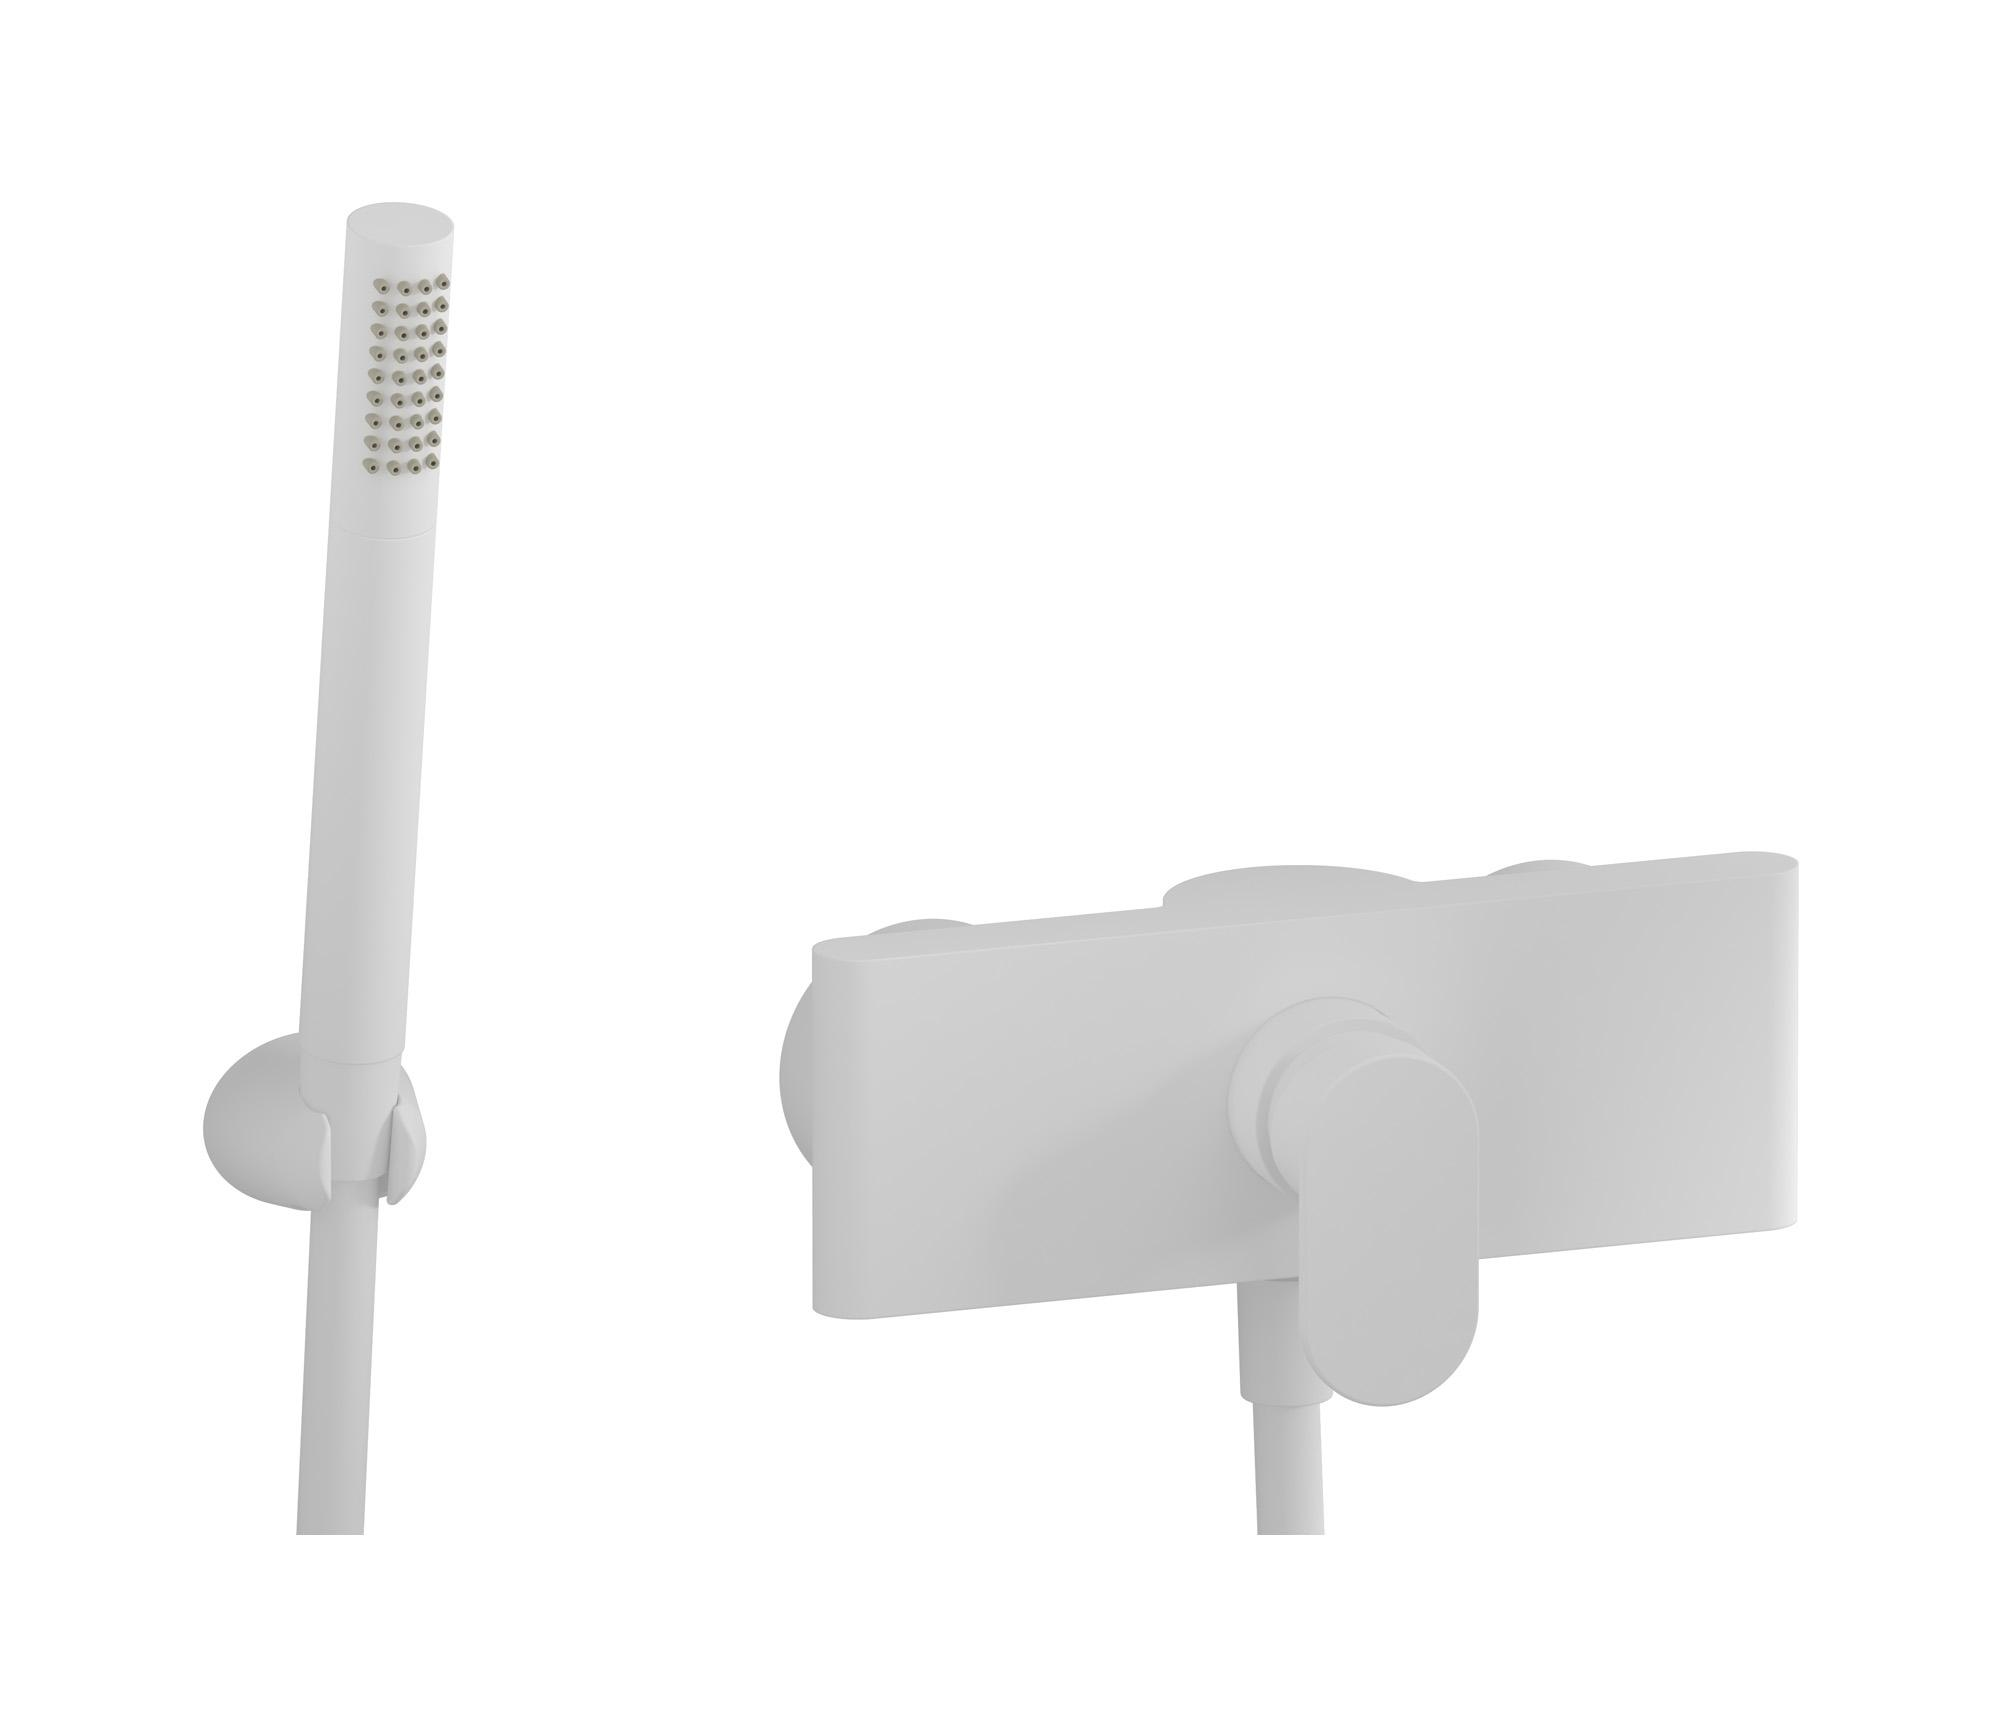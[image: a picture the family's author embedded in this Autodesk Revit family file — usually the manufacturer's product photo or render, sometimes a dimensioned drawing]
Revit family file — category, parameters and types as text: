
# Revit family: K2350
name_source: partatom
category: Apparecchi idraulici
units: mm (PartAtom-declared; Revit-internal decimal feet)

## family parameters
Basato su piano di lavoro = No
Condiviso = No
Mantieni orientamento annotazione = No
Numero OmniClass = 23.45.55.17
Punto di calcolo locali = No
Quota connettore circolare = Usa diametro
Sempre verticale = Sì
Taglio con vuoti quando caricato = No
Tipo di parte = Normale
Titolo OmniClass = Mixing Faucets

## types (9) — shared parameters
Cold water inlet = 10 mm  [stored 0.0328084 ft]
Commenti sul tipo = Shower mixer
Connessione CW = No
Connessione HW = No
Connessione di scarico = No
Connessione di ventilazione = No
Descrizione = Wall mounted shower mixer with shower kit
Hot water inlet = 10 mm  [stored 0.0328084 ft]
Produttore = IB Rubinetterie S.p.A.
URL = https://www.weareib.it
zero-valued in all types: Prospetto di default

## per-type parameters (varying)
| type | Finishes surface | Immagine tipo | Modello |
| Chrome | IB_Chrome | K2350CC.jpg | K2350CC |
| Matt black | IB_matt black | K2350NP.jpg | K2350NP |
| Matt white | IB_matt white | K2350BO.jpg | K2350BO |
| Platinum | IB_Platinum | K2350PL.jpg | K2350PL |
| Brushed nickel | IB_Brushed nickel | K2350SS.jpg | K2350SS |
| Pale gold | IB_Pale gold | K2350II.jpg | K2350II |
| Brushed pale gold | IB_brushed pale gold | K2350IS.jpg | K2350IS |
| Rose gold | IB_Rose gold | K2350RS.jpg | K2350RS |
| Gold | IB_gold | K2350OO.jpg | K2350OO |

note: [stored X ft] marks values corroborated as IEEE doubles in the binary element streams (Revit-internal decimal feet)
